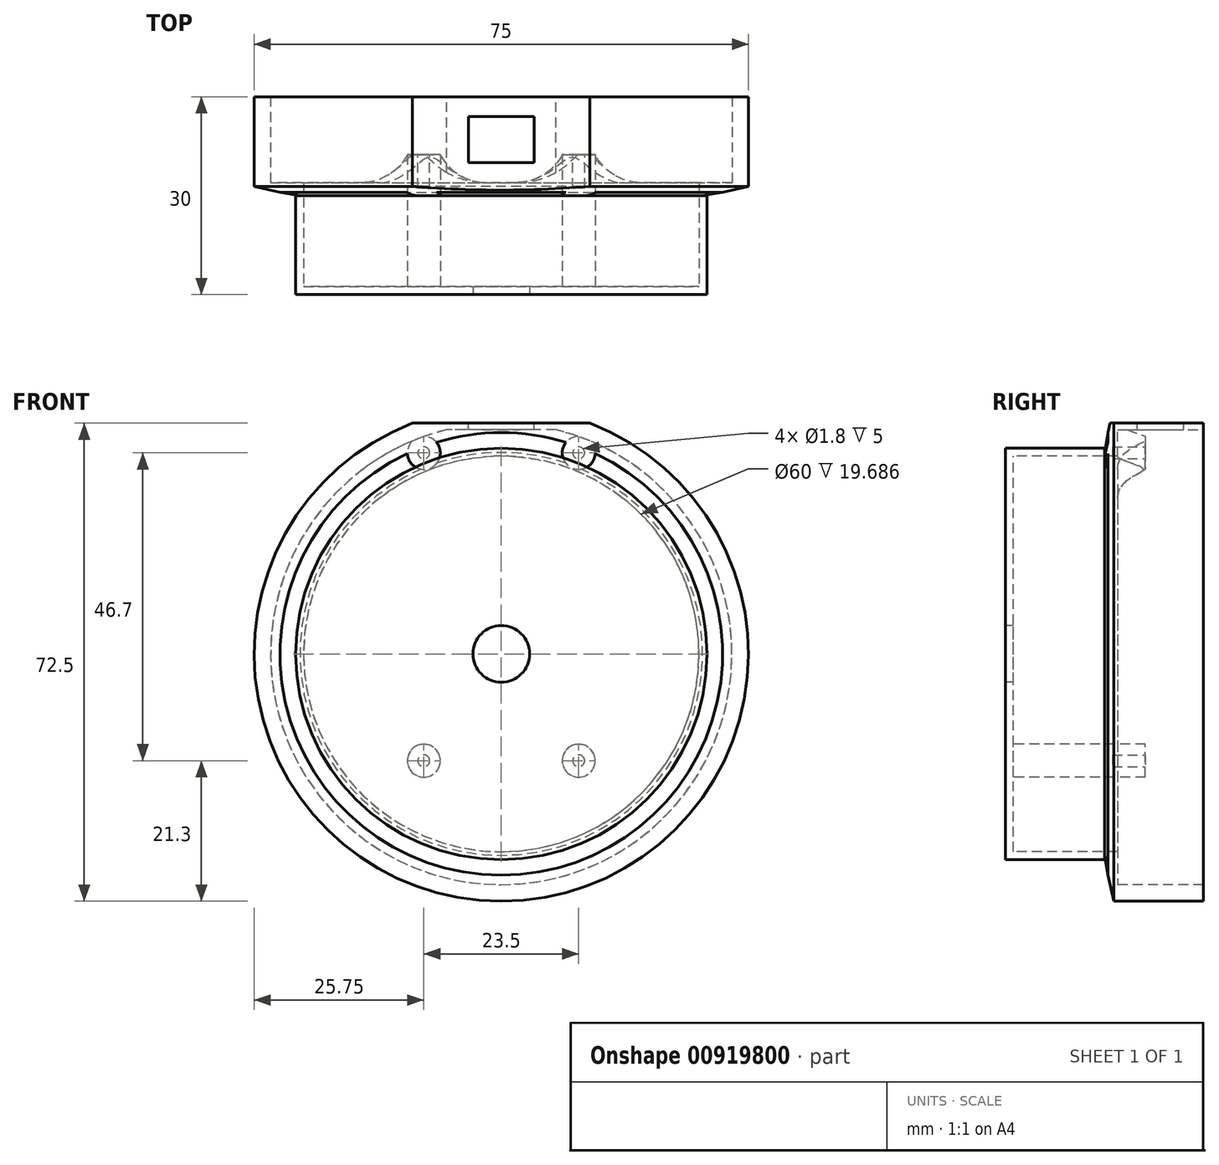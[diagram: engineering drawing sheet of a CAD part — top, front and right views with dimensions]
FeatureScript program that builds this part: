
annotation { "Feature Type Name" : "Feature", "Feature Type Description" : "" }
export const myFeature = defineFeature(function(context is Context, id is Id, definition is map)
    precondition{}
    {
        {
            var Q0;
            Q0=qCreatedBy(makeId("Front.planeOp"),FACE);
            var sketch = newSketch(context, id + "F0", { "sketchPlane" : qUnion([Q0])});
            skCircle(sketch, "E0", {"center": v(0, 0) * mm, "radius": 37.5 * mm});
            skSolve(sketch);
        }
        {
            var Q0;
            Q0=makeQuery(id+"F0.imprint","IMPRINT",FACE,{"disambiguationData":[TD([[makeQuery(id+"F0.imprint","IMPRINT",EDGE,{"derivedFrom":sQuery(id+"F0.wireOp",EDGE,"E0")}),1.0]])]});
            extrude(context, id + "F1", {"entities" : qUnion([Q0]), "depth" : 30 * mm, "offsetDistance" : 25 * mm});
        }
        {
            var Q0;
            Q0=makeQuery(id+"F1.opExtrude","CAP_FACE",FACE,{"disambiguationData":[OSD([sQuery(id+"F0.wireOp",EDGE,"E0")])],"isStart":false});
            var sketch = newSketch(context, id + "F2", { "sketchPlane" : qUnion([Q0])});
            skCircle(sketch, "E1", {"center": v(0, 0) * mm, "radius": 31.2 * mm});
            skSolve(sketch);
        }
        {
            var Q0;
            Q0=makeQuery(id+"F2.imprint","IMPRINT",FACE,{"disambiguationData":[TD([[makeQuery(id+"F2.imprint","IMPRINT",EDGE,{"derivedFrom":sQuery(id+"F2.wireOp",EDGE,"E1")}),-1.0]])]});
            extrude(context, id + "F3", {"entities" : qUnion([Q0]), "operationType" : NewBodyOperationType.REMOVE, "oppositeDirection" : true, "depth" : 15 * mm, "offsetDistance" : 25 * mm});
        }
        {
            var Q0;
            Q0=makeQuery(id+"F1.opExtrude","CAP_FACE",FACE,{"disambiguationData":[OSD([sQuery(id+"F0.wireOp",EDGE,"E0")])],"isStart":false});
            var sketch = newSketch(context, id + "F4", { "sketchPlane" : qUnion([Q0])});
            skCircle(sketch, "E2", {"center": v(0, 0) * mm, "radius": 4.3 * mm});
            skSolve(sketch);
        }
        {
            var Q0;
            Q0 = qSketchRegion(id + "F4", true);
            extrude(context, id + "F5", {"entities" : qUnion([Q0]), "operationType" : NewBodyOperationType.REMOVE, "endBound" : BoundingType.THROUGH_ALL, "oppositeDirection" : true, "depth" : 25 * mm, "offsetDistance" : 25 * mm});
        }
        {
            var Q0;
            Q0=qCreatedBy(makeId("Top.planeOp"),FACE);
            var sketch = newSketch(context, id + "F6", { "sketchPlane" : qUnion([Q0])});
            skLineSegment(sketch, "E3", {"start": v(0, -28.8) * mm, "end": v(-30, -28.8) * mm});
            skLineSegment(sketch, "E4", {"start": v(-30, -28.8) * mm, "end": v(-30, -13) * mm});
            skLineSegment(sketch, "E5", {"start": v(-30, -13) * mm, "end": v(-35, -13) * mm});
            skLineSegment(sketch, "E6", {"start": v(-35, -13) * mm, "end": v(-35, 0) * mm});
            skLineSegment(sketch, "E7", {"start": v(-35, 0) * mm, "end": v(0, 0) * mm});
            skLineSegment(sketch, "E8", {"start": v(0, 0) * mm, "end": v(0, -28.8) * mm});
            skLineSegment(sketch, "E9", {"start": v(-30.54, -15) * mm, "end": v(-38.37, -13.62) * mm});
            skLineSegment(sketch, "E10", {"start": v(-38.37, -13.62) * mm, "end": v(-38.37, -15) * mm});
            skLineSegment(sketch, "E11", {"start": v(-38.37, -15) * mm, "end": v(-30.54, -15) * mm});
            skLineSegment(sketch, "E12", {"start": v(0, 32.19) * mm, "end": v(0, -55.61) * mm, "construction": true});
            skSolve(sketch);
        }
        {
            var Q0;
            Q0 = qSketchRegion(id + "F6", true);
            var Q1;
            Q1=sQuery(id+"F6.wireOp",EDGE,"E12");
            revolve(context, id + "F7", {"operationType" : NewBodyOperationType.REMOVE, "surfaceOperationType" : NewSurfaceOperationType.NEW, "entities" : qUnion([Q0]), "axis" : qUnion([Q1]), "revolveType" : RevolveType.FULL, "oppositeDirection" : true});
        }
        {
            var Q0;
            Q0=makeQuery(id+"F1.opExtrude","CAP_FACE",FACE,{"disambiguationData":[OSD([sQuery(id+"F0.wireOp",EDGE,"E0")])],"isStart":true});
            var sketch = newSketch(context, id + "F8", { "sketchPlane" : qUnion([Q0])});
            skLineSegment(sketch, "E13", {"start": v(-8.3, 34) * mm, "end": v(8.3, 34) * mm});
            skArc(sketch, "E14", {"start": v(8.3, 34) * mm, "mid": v(0, 35) * mm, "end": v(-8.3, 34) * mm});
            skSolve(sketch);
        }
        {
            var Q0;
            Q0 = qSketchRegion(id + "F8", true);
            extrude(context, id + "F9", {"entities" : qUnion([Q0]), "operationType" : NewBodyOperationType.ADD, "oppositeDirection" : true, "depth" : 14 * mm, "offsetDistance" : 25 * mm});
        }
        {
            var Q0;
            Q0=makeQuery(id+"F9.boolean.opBoolean","MERGE",FACE,{"derivedFrom":[makeQuery(id+"F1.opExtrude","CAP_FACE",FACE,{"disambiguationData":[OSD([sQuery(id+"F0.wireOp",EDGE,"E0")])],"isStart":true}),makeQuery(id+"F9.opExtrude","CAP_FACE",FACE,{"disambiguationData":[OSD([sQuery(id+"F8.wireOp",EDGE,"E13"),sQuery(id+"F8.wireOp",EDGE,"E14")])],"isStart":true})]});
            var sketch = newSketch(context, id + "F10", { "sketchPlane" : qUnion([Q0])});
            skLineSegment(sketch, "E15.bottom", {"start": v(-29.91, 41.45) * mm, "end": v(25.45, 41.45) * mm});
            skLineSegment(sketch, "E15.top", {"start": v(-29.91, 35) * mm, "end": v(25.45, 35) * mm});
            skLineSegment(sketch, "E15.left", {"start": v(-29.91, 41.45) * mm, "end": v(-29.91, 35) * mm});
            skLineSegment(sketch, "E15.right", {"start": v(25.45, 41.45) * mm, "end": v(25.45, 35) * mm});
            skSolve(sketch);
        }
        {
            var Q0;
            Q0 = qSketchRegion(id + "F10", true);
            extrude(context, id + "F11", {"entities" : qUnion([Q0]), "operationType" : NewBodyOperationType.REMOVE, "endBound" : BoundingType.THROUGH_ALL, "oppositeDirection" : true, "depth" : 25 * mm, "offsetDistance" : 25 * mm});
        }
        {
            var Q0;
            Q0=makeQuery(id+"F11.boolean.opBoolean","COPY",FACE,{"derivedFrom":makeQuery(id+"F11.opExtrude","SWEPT_FACE",FACE,{"disambiguationData":[OSD([sQuery(id+"F10.wireOp",EDGE,"E15.top")])]})});
            var sketch = newSketch(context, id + "F12", { "sketchPlane" : qUnion([Q0])});
            skLineSegment(sketch, "E16.bottom", {"start": v(-5, -3) * mm, "end": v(5, -3) * mm});
            skLineSegment(sketch, "E16.top", {"start": v(-5, -10) * mm, "end": v(5, -10) * mm});
            skLineSegment(sketch, "E16.left", {"start": v(-5, -3) * mm, "end": v(-5, -10) * mm});
            skLineSegment(sketch, "E16.right", {"start": v(5, -3) * mm, "end": v(5, -10) * mm});
            skSolve(sketch);
        }
        {
            var Q0;
            Q0 = qSketchRegion(id + "F12", true);
            extrude(context, id + "F13", {"entities" : qUnion([Q0]), "operationType" : NewBodyOperationType.REMOVE, "oppositeDirection" : true, "depth" : 25 * mm, "offsetDistance" : 25 * mm});
        }
        {
            var Q0;
            Q0=makeQuery(id+"F7.boolean.opBoolean","COPY",FACE,{"derivedFrom":makeQuery(id+"F7.opRevolve","SWEPT_FACE",FACE,{"disambiguationData":[OSD([sQuery(id+"F6.wireOp",EDGE,"E3")])]})});
            var sketch = newSketch(context, id + "F14", { "sketchPlane" : qUnion([Q0])});
            skLineSegment(sketch, "E17.bottom", {"start": v(-11.75, 30.5) * mm, "end": v(11.75, 30.5) * mm, "construction": true});
            skLineSegment(sketch, "E17.top", {"start": v(-11.75, -16.2) * mm, "end": v(11.75, -16.2) * mm, "construction": true});
            skLineSegment(sketch, "E17.left", {"start": v(-11.75, 30.5) * mm, "end": v(-11.75, -16.2) * mm, "construction": true});
            skLineSegment(sketch, "E17.right", {"start": v(11.75, 30.5) * mm, "end": v(11.75, -16.2) * mm, "construction": true});
            skCircle(sketch, "E18", {"center": v(11.75, 30.5) * mm, "radius": 2.5 * mm});
            skCircle(sketch, "E19", {"center": v(-11.75, 30.5) * mm, "radius": 2.5 * mm});
            skCircle(sketch, "E20", {"center": v(11.75, -16.2) * mm, "radius": 2.5 * mm});
            skCircle(sketch, "E21", {"center": v(-11.75, -16.2) * mm, "radius": 2.5 * mm});
            skSolve(sketch);
        }
        {
            var Q0;
            Q0 = qSketchRegion(id + "F14", true);
            extrude(context, id + "F15", {"entities" : qUnion([Q0]), "operationType" : NewBodyOperationType.ADD, "depth" : 20 * mm, "offsetDistance" : 25 * mm});
        }
        {
            var Q0;
            Q0=makeQuery(id+"F1.opExtrude","CAP_FACE",FACE,{"disambiguationData":[OSD([sQuery(id+"F0.wireOp",EDGE,"E0")])],"isStart":false});
            var sketch = newSketch(context, id + "F16", { "sketchPlane" : qUnion([Q0])});
            skCircle(sketch, "E22", {"center": v(0, 0) * mm, "radius": 42.1 * mm});
            skSolve(sketch);
        }
        {
            var Q0;
            Q0=makeQuery(id+"F16.imprint","IMPRINT",FACE,{"disambiguationData":[TD([[makeQuery(id+"F16.imprint","IMPRINT",EDGE,{"derivedFrom":sQuery(id+"F16.wireOp",EDGE,"E22")}),1.0]])]});
            extrude(context, id + "F17", {"entities" : qUnion([Q0]), "operationType" : NewBodyOperationType.REMOVE, "oppositeDirection" : true, "depth" : 15 * mm, "offsetDistance" : 25 * mm});
        }
        {
            var Q0;
            Q0=makeQuery(id+"F15.opExtrude","CAP_FACE",FACE,{"disambiguationData":[OSD([sQuery(id+"F14.wireOp",EDGE,"E19")])],"isStart":false});
            var sketch = newSketch(context, id + "F18", { "sketchPlane" : qUnion([Q0])});
            skCircle(sketch, "E23", {"center": v(-11.75, 30.5) * mm, "radius": 0.9 * mm});
            skLineSegment(sketch, "E24", {"start": v(-11.75, 30.5) * mm, "end": v(27.46, 30.5) * mm, "construction": true});
            skLineSegment(sketch, "E25", {"start": v(-11.75, 30.5) * mm, "end": v(-11.75, -22.78) * mm, "construction": true});
            skLineSegment(sketch, "E26", {"start": v(-11.75, -16.2) * mm, "end": v(15.96, -16.2) * mm, "construction": true});
            skLineSegment(sketch, "E27", {"start": v(11.75, 30.5) * mm, "end": v(11.75, -16.2) * mm, "construction": true});
            skCircle(sketch, "E28", {"center": v(11.75, 30.5) * mm, "radius": 0.9 * mm});
            skCircle(sketch, "E29", {"center": v(11.75, -16.2) * mm, "radius": 0.9 * mm});
            skCircle(sketch, "E30", {"center": v(-11.75, -16.2) * mm, "radius": 0.9 * mm});
            skSolve(sketch);
        }
        {
            var Q0;
            Q0 = qSketchRegion(id + "F18", true);
            extrude(context, id + "F19", {"entities" : qUnion([Q0]), "operationType" : NewBodyOperationType.REMOVE, "oppositeDirection" : true, "depth" : 5 * mm, "offsetDistance" : 25 * mm});
        }
        {
            var Q0;
            Q0=makeQuery(id+"F15.opExtrude","CAP_EDGE",EDGE,{"disambiguationData":[OSD([sQuery(id+"F14.wireOp",EDGE,"E21")])],"isStart":true});
            var Q1;
            Q1=makeQuery(id+"F15.opExtrude","CAP_EDGE",EDGE,{"disambiguationData":[OSD([sQuery(id+"F14.wireOp",EDGE,"E20")])],"isStart":true});
            var Q2;
            Q2=makeQuery(id+"F15.boolean.opBoolean","INTERSECT",EDGE,{"derivedFrom":[makeQuery(id+"F7.boolean.opBoolean","COPY",FACE,{"derivedFrom":makeQuery(id+"F7.opRevolve","SWEPT_FACE",FACE,{"disambiguationData":[OSD([sQuery(id+"F6.wireOp",EDGE,"E5")])]})}),makeQuery(id+"F15.opExtrude","SWEPT_FACE",FACE,{"disambiguationData":[OSD([sQuery(id+"F14.wireOp",EDGE,"E19")])]})]});
            var Q3;
            Q3=makeQuery(id+"F15.boolean.opBoolean","INTERSECT",EDGE,{"derivedFrom":[makeQuery(id+"F7.boolean.opBoolean","COPY",FACE,{"derivedFrom":makeQuery(id+"F7.opRevolve","SWEPT_FACE",FACE,{"disambiguationData":[OSD([sQuery(id+"F6.wireOp",EDGE,"E5")])]})}),makeQuery(id+"F15.opExtrude","SWEPT_FACE",FACE,{"disambiguationData":[OSD([sQuery(id+"F14.wireOp",EDGE,"E18")])]})]});
            fillet(context, id + "F20", {"entities" : qUnion([Q0, Q1, Q2, Q3]), "radius" : 8 * mm, "tangentPropagation" : true, "allowEdgeOverflow" : false});
        }
        {
            var Q0;
            Q0=qCreatedBy(makeId("Right.planeOp"),FACE);
            var sketch = newSketch(context, id + "F21", { "sketchPlane" : qUnion([Q0])});
            skLineSegment(sketch, "E31", {"start": v(18.95, 0) * mm, "end": v(-57.36, 0) * mm, "construction": true});
            skLineSegment(sketch, "E32", {"start": v(-12.7, 41.42) * mm, "end": v(-15, 31.2) * mm});
            skLineSegment(sketch, "E33", {"start": v(-21.17, 31.2) * mm, "end": v(-21.17, 41.92) * mm});
            skLineSegment(sketch, "E34", {"start": v(-12.7, 41.42) * mm, "end": v(-21.17, 41.92) * mm});
            skLineSegment(sketch, "E35", {"start": v(-15, 31.2) * mm, "end": v(-21.17, 31.2) * mm});
            skSolve(sketch);
        }
        {
            var Q0;
            Q0 = qSketchRegion(id + "F21", true);
            var Q1;
            Q1=sQuery(id+"F21.wireOp",EDGE,"E31");
            revolve(context, id + "F22", {"operationType" : NewBodyOperationType.REMOVE, "surfaceOperationType" : NewSurfaceOperationType.NEW, "entities" : qUnion([Q0]), "axis" : qUnion([Q1]), "revolveType" : RevolveType.FULL, "oppositeDirection" : true});
        }
    });
